# Revit family: Accesoories-Teknion-YERD_Recessed_Module_Access_Door-R2022
name_source: partatom
category: Furniture
units: mm (PartAtom-declared; Revit-internal decimal feet)

## family parameters
Always vertical = Yes
Cut with Voids When Loaded = No
Enable Cutting in Views = No
OmniClass Number = 23.40.20.00
OmniClass Title = General Furniture and Specialties
Render Appearance Source = Family Geometry
Room Calculation Point = No
Shared = Yes
Work Plane-Based = No

## types (2) — shared parameters
Assembly Code = E2020200
Manufacturer = Teknion
Manufacturer Fax = 416.661.4586
Part Number = YERD
Product Documentation Link = https://www.teknion.com
Product Line = Complements
Product Page URL = https://www.teknion.com
Sustainability Data = https://www.teknion.com
URL = www.teknion.com
Unit Weight URL = http://www.teknion.com
Warranty = http://www.teknion.com
zero-valued in all types: Default Elevation

## per-type parameters (varying)
| type | Description | Length | Model |
| 12" Standard Electric Cutout | Recessed Module - Access Door, 12" Standard Electric Cutout | 12.055 " | YERDAE |
| 7" Standard Electric Cutout | Recessed Module - Access Door, 7" Standard Electric Cutout | 7.016 " | YERDAA |

## geometry (parser evidence)
native form markers: Sweep x2
no freeform markers — native parametric forms only
